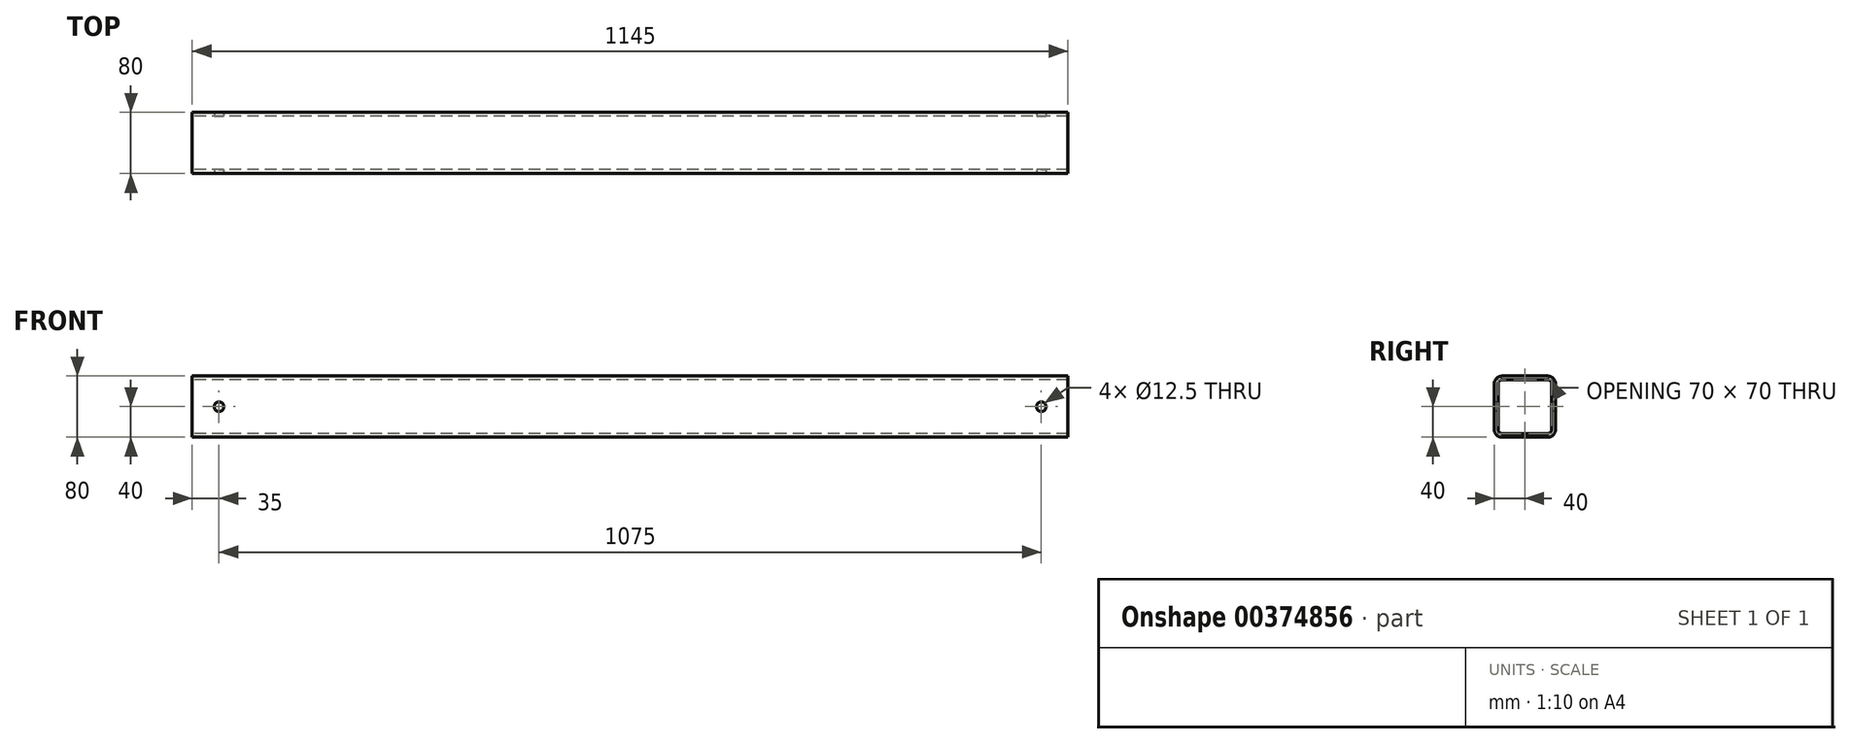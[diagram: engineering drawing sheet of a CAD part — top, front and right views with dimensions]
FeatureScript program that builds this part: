
annotation { "Feature Type Name" : "Feature", "Feature Type Description" : "" }
export const myFeature = defineFeature(function(context is Context, id is Id, definition is map)
    precondition{}
    {
        {
            var Q0;
            Q0=qCreatedBy(makeId("Right.planeOp"),FACE);
            var sketch = newSketch(context, id + "F0", { "sketchPlane" : qUnion([Q0])});
            skLineSegment(sketch, "E0.bottom", {"start": v(30, 40) * mm, "end": v(-30, 40) * mm});
            skLineSegment(sketch, "E0.top", {"start": v(30, -40) * mm, "end": v(-30, -40) * mm});
            skLineSegment(sketch, "E0.left", {"start": v(40, 30) * mm, "end": v(40, -30) * mm});
            skLineSegment(sketch, "E0.right", {"start": v(-40, 30) * mm, "end": v(-40, -30) * mm});
            skPoint(sketch, "E0.middle", {"position": v(0, 0) * mm});
            skPoint(sketch, "E1.visualSharp", {"position": v(-40, 40) * mm});
            skArc(sketch, "E1.filletArc", {"start": v(-30, 40) * mm, "mid": v(-37.07, 37.07) * mm, "end": v(-40, 30) * mm});
            skPoint(sketch, "E2.visualSharp", {"position": v(40, 40) * mm});
            skArc(sketch, "E2.filletArc", {"start": v(40, 30) * mm, "mid": v(37.07, 37.07) * mm, "end": v(30, 40) * mm});
            skPoint(sketch, "E3.visualSharp", {"position": v(40, -40) * mm});
            skArc(sketch, "E3.filletArc", {"start": v(30, -40) * mm, "mid": v(37.07, -37.07) * mm, "end": v(40, -30) * mm});
            skPoint(sketch, "E4.visualSharp", {"position": v(-40, -40) * mm});
            skArc(sketch, "E4.filletArc", {"start": v(-40, -30) * mm, "mid": v(-37.07, -37.07) * mm, "end": v(-30, -40) * mm});
            skArc(sketch, "E5.0", {"start": v(35, 30) * mm, "mid": v(33.54, 33.54) * mm, "end": v(30, 35) * mm});
            skLineSegment(sketch, "E5.1", {"start": v(35, 30) * mm, "end": v(35, -30) * mm});
            skLineSegment(sketch, "E5.2", {"start": v(30, 35) * mm, "end": v(-30, 35) * mm});
            skArc(sketch, "E5.3", {"start": v(30, -35) * mm, "mid": v(33.54, -33.54) * mm, "end": v(35, -30) * mm});
            skArc(sketch, "E5.4", {"start": v(-30, 35) * mm, "mid": v(-33.54, 33.54) * mm, "end": v(-35, 30) * mm});
            skLineSegment(sketch, "E5.5", {"start": v(-35, 30) * mm, "end": v(-35, -30) * mm});
            skArc(sketch, "E5.6", {"start": v(-35, -30) * mm, "mid": v(-33.54, -33.54) * mm, "end": v(-30, -35) * mm});
            skLineSegment(sketch, "E5.7", {"start": v(30, -35) * mm, "end": v(-30, -35) * mm});
            skSolve(sketch);
        }
        {
            var Q0;
            Q0 = qSketchRegion(id + "F0", true);
            extrude(context, id + "F1", {"entities" : qUnion([Q0]), "endBound" : BoundingType.SYMMETRIC, "depth" : 1145 * mm});
        }
        {
            var Q0;
            Q0=makeQuery(id+"F1.opExtrude","SWEPT_FACE",FACE,{"disambiguationData":[OSD([sQuery(id+"F0.wireOp",EDGE,"E0.right")])]});
            var sketch = newSketch(context, id + "F2", { "sketchPlane" : qUnion([Q0])});
            skCircle(sketch, "E6", {"center": v(537.5, 0) * mm, "radius": 6.25 * mm});
            skPoint(sketch, "E6.centerSnap0", {"position": v(572.5, 0) * mm});
            skCircle(sketch, "E7", {"center": v(-537.5, 0) * mm, "radius": 6.25 * mm});
            skPoint(sketch, "E7.centerSnap0", {"position": v(-572.5, 0) * mm});
            skSolve(sketch);
        }
        {
            var Q0;
            Q0 = qSketchRegion(id + "F2", true);
            extrude(context, id + "F3", {"entities" : qUnion([Q0]), "operationType" : NewBodyOperationType.REMOVE, "endBound" : BoundingType.THROUGH_ALL, "oppositeDirection" : true, "depth" : 25 * mm});
        }
    });
